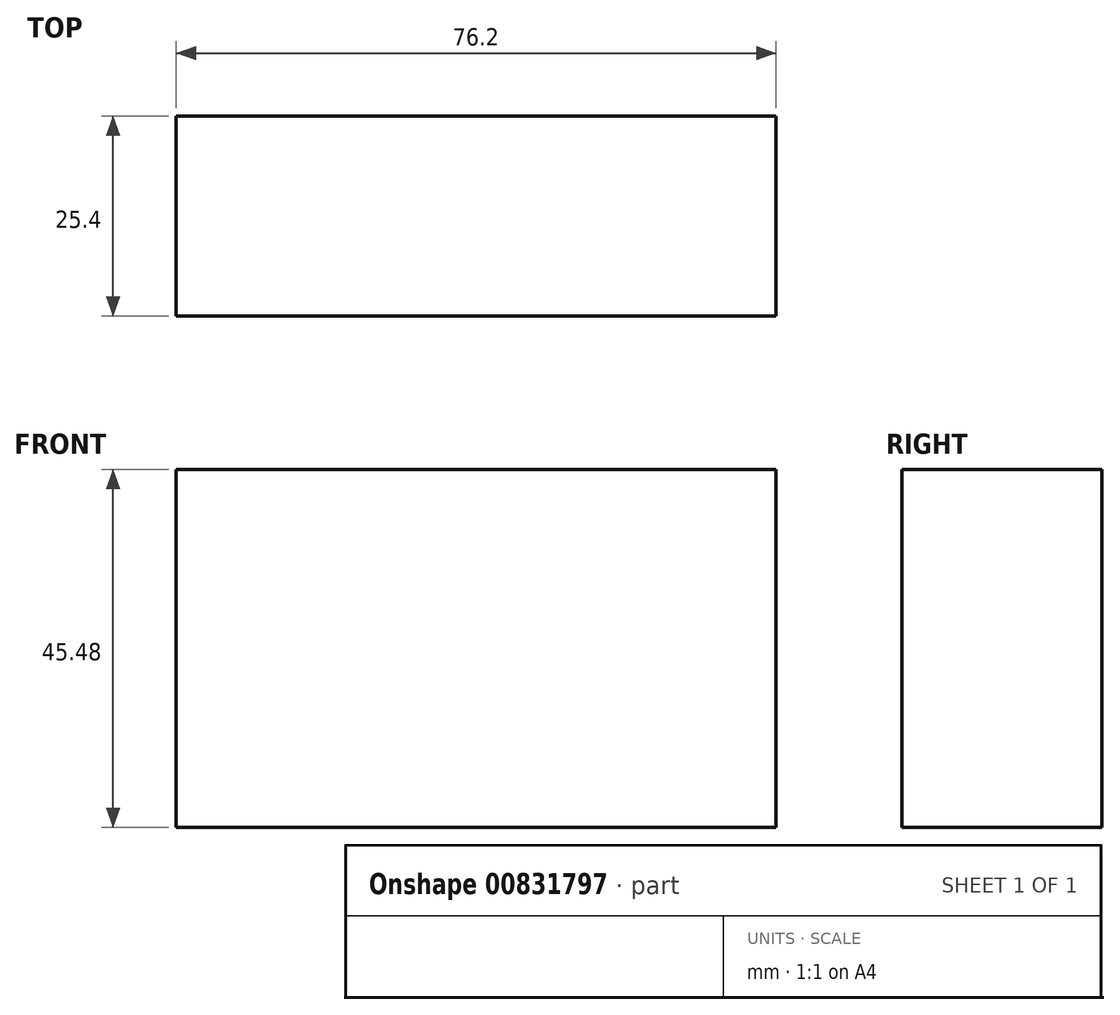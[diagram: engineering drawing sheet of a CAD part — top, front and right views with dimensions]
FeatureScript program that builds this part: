
annotation { "Feature Type Name" : "Feature", "Feature Type Description" : "" }
export const myFeature = defineFeature(function(context is Context, id is Id, definition is map)
    precondition{}
    {
        {
            var Q0;
            Q0=qCreatedBy(makeId("Front.planeOp"),FACE);
            var sketch = newSketch(context, id + "F0", { "sketchPlane" : qUnion([Q0])});
            skLineSegment(sketch, "E0.bottom", {"start": v(-76.2, 63.14) * mm, "end": v(0, 63.14) * mm});
            skLineSegment(sketch, "E0.top", {"start": v(-76.2, 17.66) * mm, "end": v(0, 17.66) * mm});
            skLineSegment(sketch, "E0.left", {"start": v(-76.2, 63.14) * mm, "end": v(-76.2, 17.66) * mm});
            skLineSegment(sketch, "E0.right", {"start": v(0, 63.14) * mm, "end": v(0, 17.66) * mm});
            skSolve(sketch);
        }
        {
            var Q0;
            Q0=makeQuery(id+"F0.imprint","IMPRINT",FACE,{"disambiguationData":[TD([[makeQuery(id+"F0.imprint","IMPRINT",EDGE,{"derivedFrom":sQuery(id+"F0.wireOp",EDGE,"E0.bottom")}),-1.0]])]});
            extrude(context, id + "F1", {"entities" : qUnion([Q0]), "depth" : 25.4 * mm, "offsetDistance" : 25.4 * mm});
        }
    });
